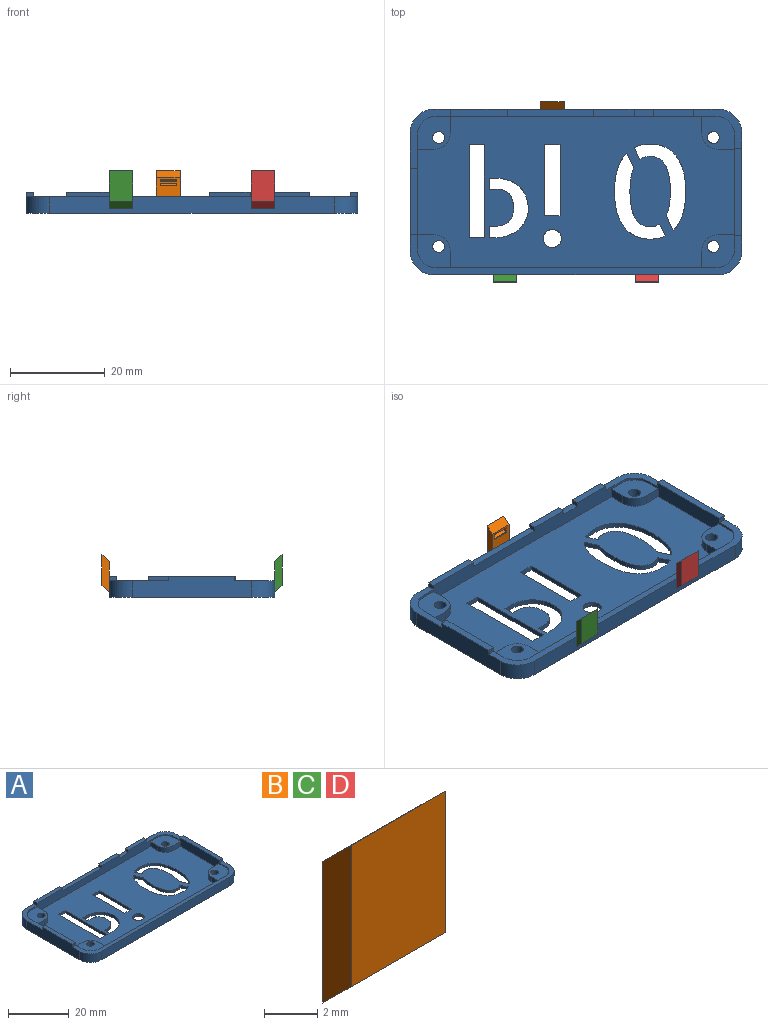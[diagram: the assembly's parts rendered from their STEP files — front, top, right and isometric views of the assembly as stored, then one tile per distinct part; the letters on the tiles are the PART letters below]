
ASSEMBLY  parts=4 mates=3
PART A: 129 faces, bbox 70x35x4.5 mm
  f0: plane 70x35mm, normal (0,0,-1), area 2104.1mm2, adj f7,f8,f9,f10,f31,f32,f33,f34
  f1: plane 67x32mm, normal (0,0,1), area 1653.8mm2, adj f11,f13,f14,f15,f17,f18,f19,f20
  f2: plane 70x8.54mm, normal (0,0,1), area 121.8mm2, adj f8,f9,f10,f18,f19,f22,f29,f30
  f3: plane 10.15x8.25mm, normal (0,0,1), area 23.4mm2, adj f7,f8,f20,f22,f27,f31,f41,f48
  f4: plane 4.1x1.5mm, normal (0,0,1), area 6.2mm2, adj f7,f20,f38,f42
  f5: plane 18.25x1.5mm, normal (0,0,1), area 27.4mm2, adj f7,f20,f35,f39
  f6: plane 12.46x8.5mm, normal (0,0,1), area 27.3mm2, adj f7,f10,f18,f20,f28,f34,f36,f44
  f7: plane 60x4.5mm, normal (0,1,0), area 239mm2, adj f0,f3,f4,f5,f6,f31,f34,f35
  f8: plane 25x4.5mm, normal (1,0,0), area 106mm2, adj f0,f2,f3,f31,f32,f47,f48,f49
  f9: plane 60x3.5mm, normal (0,-1,0), area 210mm2, adj f0,f2,f32,f33
  f10: plane 25x4.5mm, normal (-1,0,0), area 101.5mm2, adj f0,f2,f6,f33,f34,f44,f45,f46
  f11: plane 3.5x2mm, normal (0,1,0), area 7mm2, adj f1,f12,f22,f50
  f12: plane 7x7mm, normal (0,0,1), area 38mm2, adj f11,f13,f19,f22,f30,f50,f57
  f13: plane 3.5x2mm, normal (-1,0,0), area 7mm2, adj f1,f12,f19,f50
  f14: plane 3.5x2mm, normal (0,1,0), area 7mm2, adj f1,f18,f26,f51
  f15: plane 3.5x2mm, normal (0,-1,0), area 7mm2, adj f1,f16,f18,f52
  f16: plane 7x7mm, normal (0,0,1), area 38mm2, adj f15,f17,f18,f20,f28,f52,f56
  f17: plane 3.5x2mm, normal (1,0,0), area 7mm2, adj f1,f16,f20,f52
  f18: plane 24x3.5mm, normal (1,0,0), area 62mm2, adj f1,f2,f6,f14,f15,f16,f26,f28
  f19: plane 59x2.5mm, normal (0,1,0), area 135.5mm2, adj f1,f2,f12,f13,f25,f26,f29,f30
  f20: plane 59x3.5mm, normal (0,-1,0), area 164.5mm2, adj f1,f3,f4,f5,f6,f16,f17,f21
  f21: plane 3.5x2mm, normal (-1,0,0), area 7mm2, adj f1,f20,f24,f53
  f22: plane 24x3.5mm, normal (-1,0,0), area 66.5mm2, adj f1,f2,f3,f11,f12,f23,f24,f27
  f23: plane 3.5x2mm, normal (0,-1,0), area 7mm2, adj f1,f22,f24,f53
  f24: plane 7x7mm, normal (0,0,1), area 38mm2, adj f20,f21,f22,f23,f27,f53,f55
  f25: plane 3.5x2mm, normal (1,0,0), area 7mm2, adj f1,f19,f26,f51
  f26: plane 7x7mm, normal (0,0,1), area 38mm2, adj f14,f18,f19,f25,f29,f51,f54
  f27: cylinder r=4mm len=4mm, axis (0,0,-1), area 3.1mm2, adj f3,f20,f22,f24
  f28: cylinder r=4mm len=4mm, axis (0,0,1), area 3.1mm2, adj f6,f16,f18,f20
  f29: cylinder r=4mm len=4mm, axis (0,0,-1), area 3.1mm2, adj f2,f18,f19,f26
  f30: cylinder r=4mm len=4mm, axis (0,0,1), area 3.1mm2, adj f2,f12,f19,f22
  f31: cylinder r=5mm len=5mm, axis (0,0,1), area 27.5mm2, adj f0,f3,f7,f8
  f32: cylinder r=5mm len=5mm, axis (0,0,-1), area 27.5mm2, adj f0,f2,f8,f9
  f33: cylinder r=5mm len=5mm, axis (0,0,1), area 27.5mm2, adj f0,f2,f9,f10
  f34: cylinder r=5mm len=5mm, axis (0,0,-1), area 27.5mm2, adj f0,f6,f7,f10
  f35: plane 1.5x1mm, normal (1,0,0), area 1.5mm2, adj f5,f7,f20,f37
  f36: plane 1.5x1mm, normal (-1,0,0), area 1.5mm2, adj f6,f7,f20,f37
  f37: plane 12x1.5mm, normal (0,0,1), area 18mm2, adj f7,f20,f35,f36
  f38: plane 1.5x1mm, normal (1,0,0), area 1.5mm2, adj f4,f7,f20,f40
  f39: plane 1.5x1mm, normal (-1,0,0), area 1.5mm2, adj f5,f7,f20,f40
  f40: plane 8.5x1.5mm, normal (0,0,1), area 12.8mm2, adj f7,f20,f38,f39
  f41: plane 1.5x1mm, normal (1,0,0), area 1.5mm2, adj f3,f7,f20,f43
  f42: plane 1.5x1mm, normal (-1,0,0), area 1.5mm2, adj f4,f7,f20,f43
  f43: plane 8.5x1.5mm, normal (0,0,1), area 12.8mm2, adj f7,f20,f41,f42
  f44: plane 1.5x1mm, normal (0,1,0), area 1.5mm2, adj f6,f10,f18,f46
  f45: plane 1.5x1mm, normal (0,-1,0), area 1.5mm2, adj f2,f10,f18,f46
  f46: plane 14x1.5mm, normal (0,0,1), area 21mm2, adj f10,f18,f44,f45
  f47: plane 1.5x1mm, normal (0,-1,0), area 1.5mm2, adj f2,f8,f22,f49
  f48: plane 1.5x1mm, normal (0,1,0), area 1.5mm2, adj f3,f8,f22,f49
  f49: plane 18.5x1.5mm, normal (0,0,1), area 27.8mm2, adj f8,f22,f47,f48
  f50: cylinder r=3.5mm len=3.5mm, axis (0,0,1), area 11mm2, adj f1,f11,f12,f13
  f51: cylinder r=3.5mm len=3.5mm, axis (0,0,1), area 11mm2, adj f1,f14,f25,f26
  f52: cylinder r=3.5mm len=3.5mm, axis (0,0,1), area 11mm2, adj f1,f15,f16,f17
  f53: cylinder r=3.5mm len=3.5mm, axis (0,0,1), area 11mm2, adj f1,f21,f23,f24
  f54: cylinder r=1.25mm len=3mm, axis (0,0,1), area 23.6mm2, adj f0,f26
  f55: cylinder r=1.25mm len=3mm, axis (0,0,1), area 23.6mm2, adj f0,f24
  f56: cylinder r=1.25mm len=3mm, axis (0,0,1), area 23.6mm2, adj f0,f16
  f57: cylinder r=1.25mm len=3mm, axis (0,0,1), area 23.6mm2, adj f0,f12
  f58: extruded ~1.78x1mm, area 1.8mm2, adj f0,f1,f59,f73
  f59: extruded ~1.97x1mm, area 2.1mm2, adj f0,f1,f58,f60
  f60: plane 2.51x1.17mm, normal (-0.91,-0.42,0), area 2.8mm2, adj f0,f1,f59,f61
  f61: extruded ~3.22x1mm, area 3.3mm2, adj f0,f1,f60,f62
  f62: extruded ~3.13x1mm, area 3.2mm2, adj f0,f1,f61,f63
  f63: extruded ~2.37x1.9mm, area 3.1mm2, adj f0,f1,f62,f64
  f64: extruded ~3.13x1.49mm, area 3.5mm2, adj f0,f1,f63,f65
  f65: extruded ~4.35x1mm, area 4.4mm2, adj f0,f1,f64,f66
  f66: extruded ~4.86x1mm, area 4.9mm2, adj f0,f1,f65,f67
  f67: extruded ~3.26x1.89mm, area 3.8mm2, adj f0,f1,f66,f68
  f68: plane 3.11x1.46mm, normal (-0.91,-0.42,0), area 3.4mm2, adj f0,f1,f67,f69
  f69: extruded ~2.13x1mm, area 2.2mm2, adj f0,f1,f68,f70
  f70: extruded ~2.88x1mm, area 2.9mm2, adj f0,f1,f69,f71
  f71: extruded ~3.46x1mm, area 3.5mm2, adj f0,f1,f70,f72
  f72: extruded ~2.31x1mm, area 2.5mm2, adj f0,f1,f71,f73
  f73: extruded ~1.36x1.27mm, area 1.9mm2, adj f0,f1,f58,f72
  f74: plane 3.25x1mm, normal (0,-1,0), area 3.3mm2, adj f0,f1,f75,f77
  f75: plane 15.02x1mm, normal (-1,0,0), area 15mm2, adj f0,f1,f74,f76
  f76: plane 3.25x1mm, normal (0,1,0), area 3.3mm2, adj f0,f1,f75,f77
  f77: plane 15.02x1mm, normal (1,0,0), area 15mm2, adj f0,f1,f74,f76
  f78: extruded ~1.34x1mm, area 1.5mm2, adj f0,f1,f79,f85
  f79: extruded ~1.36x1mm, area 1.5mm2, adj f0,f1,f78,f80
  f80: extruded ~1.36x1mm, area 1.5mm2, adj f0,f1,f79,f81
  f81: extruded ~1.33x1mm, area 1.5mm2, adj f0,f1,f80,f82
  f82: extruded ~1.36x1mm, area 1.5mm2, adj f0,f1,f81,f83
  f83: extruded ~1.33x1mm, area 1.5mm2, adj f0,f1,f82,f84
  f84: extruded ~1.35x1mm, area 1.5mm2, adj f0,f1,f83,f85
  f85: extruded ~1.36x1mm, area 1.5mm2, adj f0,f1,f78,f84
  f86: extruded ~2.48x1mm, area 2.5mm2, adj f0,f1,f87,f107
  f87: plane 1.36x1mm, normal (0,1,0), area 1.4mm2, adj f0,f1,f86,f88
  f88: plane 2.42x1mm, normal (1,0,0), area 2.4mm2, adj f0,f1,f87,f89
  f89: plane 1.3x1mm, normal (0,-1,0), area 1.3mm2, adj f0,f1,f88,f90
  f90: extruded ~1.97x1mm, area 2mm2, adj f0,f1,f89,f91
  f91: extruded ~1.16x1mm, area 1.5mm2, adj f0,f1,f90,f92
  f92: extruded ~1.2x1mm, area 1.3mm2, adj f0,f1,f91,f93
  f93: extruded ~1.11x1mm, area 1.1mm2, adj f0,f1,f92,f94
  f94: extruded ~2.01x1mm, area 2mm2, adj f0,f1,f93,f95
  f95: extruded ~1.27x1mm, area 1.5mm2, adj f0,f1,f94,f96
  f96: extruded ~1.05x1mm, area 1.2mm2, adj f0,f1,f95,f97
  f97: extruded ~1.16x1mm, area 1.2mm2, adj f0,f1,f96,f98
  f98: plane 1.84x1mm, normal (0,1,0), area 1.8mm2, adj f0,f1,f97,f99
  f99: plane 2.34x1mm, normal (1,0,0), area 2.3mm2, adj f0,f1,f98,f100
  f100: plane 1.28x1mm, normal (0,-1,0), area 1.3mm2, adj f0,f1,f99,f101
  f101: extruded ~2.83x1mm, area 2.9mm2, adj f0,f1,f100,f102
  f102: extruded ~2.18x1.28mm, area 2.5mm2, adj f0,f1,f101,f103
  f103: extruded ~2.04x1.41mm, area 2.5mm2, adj f0,f1,f102,f104
  f104: extruded ~2.7x1mm, area 2.8mm2, adj f0,f1,f103,f105
  f105: extruded ~2.55x1mm, area 2.6mm2, adj f0,f1,f104,f106
  f106: extruded ~1.93x1.57mm, area 2.5mm2, adj f0,f1,f105,f107
  f107: extruded ~2.2x1.2mm, area 2.5mm2, adj f0,f1,f86,f106
  f108: extruded ~3.27x1.98mm, area 3.9mm2, adj f0,f1,f109,f124
  f109: plane 3.09x1.47mm, normal (0.9,0.43,0), area 3.4mm2, adj f0,f1,f108,f110
  f110: extruded ~1x0.05mm, area 0.1mm2, adj f0,f1,f109,f111
  f111: extruded ~2.13x1mm, area 2.2mm2, adj f0,f1,f110,f112
  f112: extruded ~2.93x1mm, area 2.9mm2, adj f0,f1,f111,f113
  f113: extruded ~3.47x1mm, area 3.5mm2, adj f0,f1,f112,f114
  f114: extruded ~2.3x1mm, area 2.5mm2, adj f0,f1,f113,f115
  f115: extruded ~1.37x1.27mm, area 1.9mm2, adj f0,f1,f114,f116
  f116: extruded ~1.8x1mm, area 1.9mm2, adj f0,f1,f115,f117
  f117: extruded ~2.08x1mm, area 2.2mm2, adj f0,f1,f116,f118
  f118: plane 2.53x1.2mm, normal (0.9,0.43,0), area 2.8mm2, adj f0,f1,f117,f119
  f119: extruded ~3.35x1mm, area 3.5mm2, adj f0,f1,f118,f120
  f120: extruded ~3.14x1mm, area 3.2mm2, adj f0,f1,f119,f121
  f121: extruded ~2.37x1.89mm, area 3.1mm2, adj f0,f1,f120,f122
  f122: extruded ~3.14x1.5mm, area 3.5mm2, adj f0,f1,f121,f123
  f123: extruded ~4.37x1mm, area 4.4mm2, adj f0,f1,f122,f124
  f124: extruded ~4.93x1mm, area 5mm2, adj f0,f1,f108,f123
  f125: plane 3.2x1mm, normal (0,1,0), area 3.2mm2, adj f0,f1,f126,f128
  f126: plane 19.63x1mm, normal (1,0,0), area 19.6mm2, adj f0,f1,f125,f127
  f127: plane 3.2x1mm, normal (0,-1,0), area 3.2mm2, adj f0,f1,f126,f128
  f128: plane 19.63x1mm, normal (-1,0,0), area 19.6mm2, adj f0,f1,f125,f127
PART B: 13 faces, bbox 5x1.5x8 mm
  f0: plane 6.5x5mm, normal (0,1,0), area 28.1mm2, adj f1,f2,f4,f5,f6,f7,f8,f9
  f1: plane 8x1.5mm, normal (1,0,0), area 9.8mm2, adj f0,f3,f4,f5
  f2: plane 8x1.5mm, normal (-1,0,0), area 9.8mm2, adj f0,f3,f4,f5
  f3: plane 6.5x5mm, normal (0,-1,0), area 32.5mm2, adj f1,f2,f4,f5
  f4: plane 5x1.5mm, normal (0,0.71,0.71), area 10.6mm2, adj f0,f1,f2,f3
  f5: plane 5x1.5mm, normal (0,-0.71,-0.71), area 10.6mm2, adj f0,f1,f2,f3
  f6: plane 3.5x0.25mm, normal (0,0,1), area 0.9mm2, adj f0,f7,f9,f12
  f7: plane 1.25x0.75mm, normal (1,0,0), area 0.7mm2, adj f0,f6,f8,f10,f11,f12
  f8: plane 3.5x0.25mm, normal (0,0,-1), area 0.9mm2, adj f0,f7,f9,f11
  f9: plane 1.25x0.75mm, normal (-1,0,0), area 0.7mm2, adj f0,f6,f8,f10,f11,f12
  f10: plane 3.5x0.25mm, normal (0,1,0), area 0.9mm2, adj f7,f9,f11,f12
  f11: plane 3.5x0.5mm, normal (0,0.71,-0.71), area 2.5mm2, adj f7,f8,f9,f10
  f12: plane 3.5x0.5mm, normal (0,0.71,0.71), area 2.5mm2, adj f6,f7,f9,f10
PART C: same geometry as B
PART D: same geometry as B
PLACE A t=(-13.7,6.87,-18.87)mm
PLACE B rot(axis=(0,0,1),180deg) t=(-18.7,24.37,-13.87)mm
PLACE C t=(-28.7,-10.63,-13.87)mm
PLACE D t=(1.3,-10.63,-13.87)mm
MATE fastened A.f9 <-> C.f0  axis (0,-1,0) through (-28.7,-10.63,-17.87)mm
MATE fastened A.f9 <-> D.f0  axis (0,-1,0) through (1.3,-10.63,-17.87)mm
MATE fastened B.f0 <-> A.f7  axis (0,-1,0) through (-18.7,24.37,-17.87)mm
